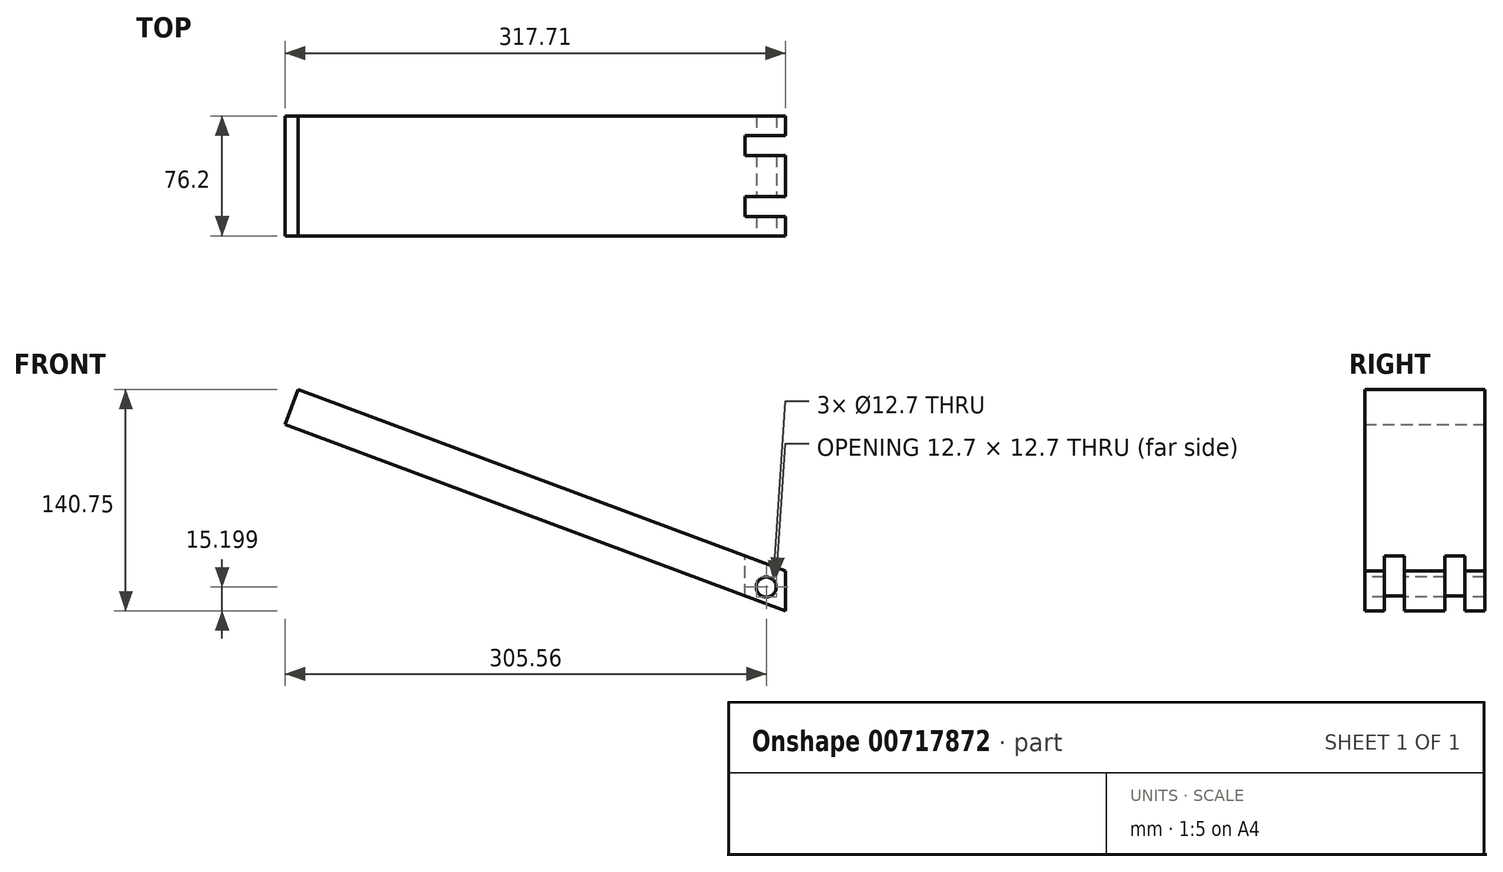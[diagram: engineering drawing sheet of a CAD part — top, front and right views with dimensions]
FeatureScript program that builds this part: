
annotation { "Feature Type Name" : "Feature", "Feature Type Description" : "" }
export const myFeature = defineFeature(function(context is Context, id is Id, definition is map)
    precondition{}
    {
        {
            var Q0;
            Q0=qCreatedBy(makeId("Front.planeOp"),FACE);
            var sketch = newSketch(context, id + "F0", { "sketchPlane" : qUnion([Q0])});
            skLineSegment(sketch, "E0", {"start": v(-119.12, 78.66) * mm, "end": v(190.28, -36.7) * mm});
            skLineSegment(sketch, "E1", {"start": v(-119.12, 78.66) * mm, "end": v(-127.44, 56.36) * mm});
            skLineSegment(sketch, "E2", {"start": v(-127.44, 56.36) * mm, "end": v(190.28, -62.1) * mm});
            skLineSegment(sketch, "E3", {"start": v(190.28, -62.1) * mm, "end": v(190.28, -36.7) * mm});
            skSolve(sketch);
        }
        {
            var Q0;
            Q0 = qSketchRegion(id + "F0", true);
            extrude(context, id + "F1", {"entities" : qUnion([Q0]), "endBound" : BoundingType.SYMMETRIC, "depth" : 76.2 * mm, "offsetDistance" : 25.4 * mm});
        }
        {
            var Q0;
            Q0=qCreatedBy(makeId("Top.planeOp"),FACE);
            var sketch = newSketch(context, id + "F2", { "sketchPlane" : qUnion([Q0])});
            skLineSegment(sketch, "E4.bottom", {"start": v(195.12, 25.7) * mm, "end": v(164.64, 25.7) * mm});
            skLineSegment(sketch, "E4.top", {"start": v(195.12, 13) * mm, "end": v(164.64, 13) * mm});
            skLineSegment(sketch, "E4.left", {"start": v(195.12, 25.7) * mm, "end": v(195.12, 13) * mm});
            skLineSegment(sketch, "E4.right", {"start": v(164.64, 25.7) * mm, "end": v(164.64, 13) * mm});
            skLineSegment(sketch, "E5.bottom", {"start": v(195.12, -12.95) * mm, "end": v(164.64, -12.95) * mm});
            skLineSegment(sketch, "E5.top", {"start": v(195.12, -25.65) * mm, "end": v(164.64, -25.65) * mm});
            skLineSegment(sketch, "E5.left", {"start": v(195.12, -12.95) * mm, "end": v(195.12, -25.65) * mm});
            skLineSegment(sketch, "E5.right", {"start": v(164.64, -12.95) * mm, "end": v(164.64, -25.65) * mm});
            skSolve(sketch);
        }
        {
            var Q0;
            Q0 = qSketchRegion(id + "F2", true);
            extrude(context, id + "F3", {"entities" : qUnion([Q0]), "operationType" : NewBodyOperationType.REMOVE, "oppositeDirection" : true, "depth" : 72.9 * mm, "offsetDistance" : 25.4 * mm});
        }
        {
            var Q0;
            Q0=qCreatedBy(makeId("Front.planeOp"),FACE);
            var sketch = newSketch(context, id + "F4", { "sketchPlane" : qUnion([Q0])});
            skCircle(sketch, "E6", {"center": v(178.13, -46.9) * mm, "radius": 6.35 * mm});
            skPoint(sketch, "E6.first.point", {"position": v(170.92, -43.05) * mm});
            skPoint(sketch, "E6.second.point", {"position": v(183.41, -45.28) * mm});
            skPoint(sketch, "E6.third.point", {"position": v(182.21, -47.85) * mm});
            skSolve(sketch);
        }
        {
            var Q0;
            Q0 = qSketchRegion(id + "F4", true);
            extrude(context, id + "F5", {"entities" : qUnion([Q0]), "operationType" : NewBodyOperationType.REMOVE, "endBound" : BoundingType.SYMMETRIC, "oppositeDirection" : true, "depth" : 76.2 * mm, "offsetDistance" : 25.4 * mm});
        }
        {
            var Q0;
            Q0=makeQuery(id+"F1.opExtrude","SWEPT_BODY",BODY,{"disambiguationData":[OSD([sQuery(id+"F0.wireOp",EDGE,"E0"),sQuery(id+"F0.wireOp",EDGE,"E1"),sQuery(id+"F0.wireOp",EDGE,"E2"),sQuery(id+"F0.wireOp",EDGE,"E3")])]});
            transform(context, id + "F6", {"entities" : qUnion([Q0]), "transformType" : TransformType.TRANSLATION_3D, "dx" : -31.5 * mm, "dy" : 0 * mm, "dz" : -8.64 * mm, "makeCopy" : false});
        }
    });
